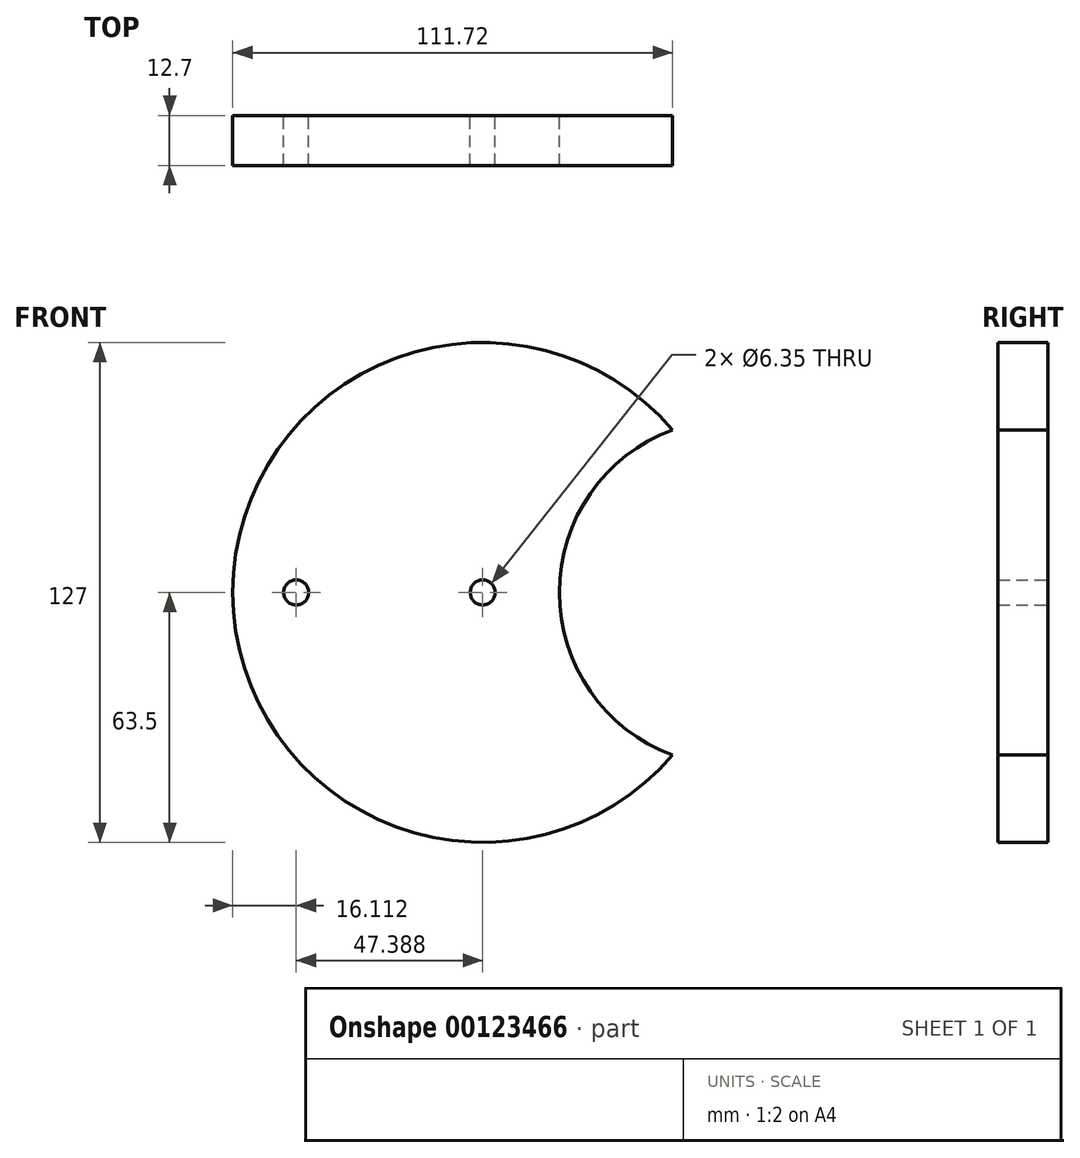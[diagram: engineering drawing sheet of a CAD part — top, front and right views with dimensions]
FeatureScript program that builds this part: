
annotation { "Feature Type Name" : "Feature", "Feature Type Description" : "" }
export const myFeature = defineFeature(function(context is Context, id is Id, definition is map)
    precondition{}
    {
        {
            var Q0;
            Q0=qCreatedBy(makeId("Front.planeOp"),FACE);
            var sketch = newSketch(context, id + "F0", { "sketchPlane" : qUnion([Q0])});
            skArc(sketch, "E0", {"start": v(48.22, 41.32) * mm, "mid": v(-63.5, 0) * mm, "end": v(48.22, -41.32) * mm});
            skArc(sketch, "E1", {"start": v(48.22, 41.32) * mm, "mid": v(19.44, 0) * mm, "end": v(48.22, -41.32) * mm});
            skCircle(sketch, "E2", {"center": v(0, 0) * mm, "radius": 3.18 * mm});
            skCircle(sketch, "E3", {"center": v(-47.39, 0) * mm, "radius": 3.18 * mm});
            skSolve(sketch);
        }
        {
            var Q0;
            Q0 = qSketchRegion(id + "F0", true);
            extrude(context, id + "F1", {"entities" : qUnion([Q0]), "depth" : 12.7 * mm});
        }
    });
